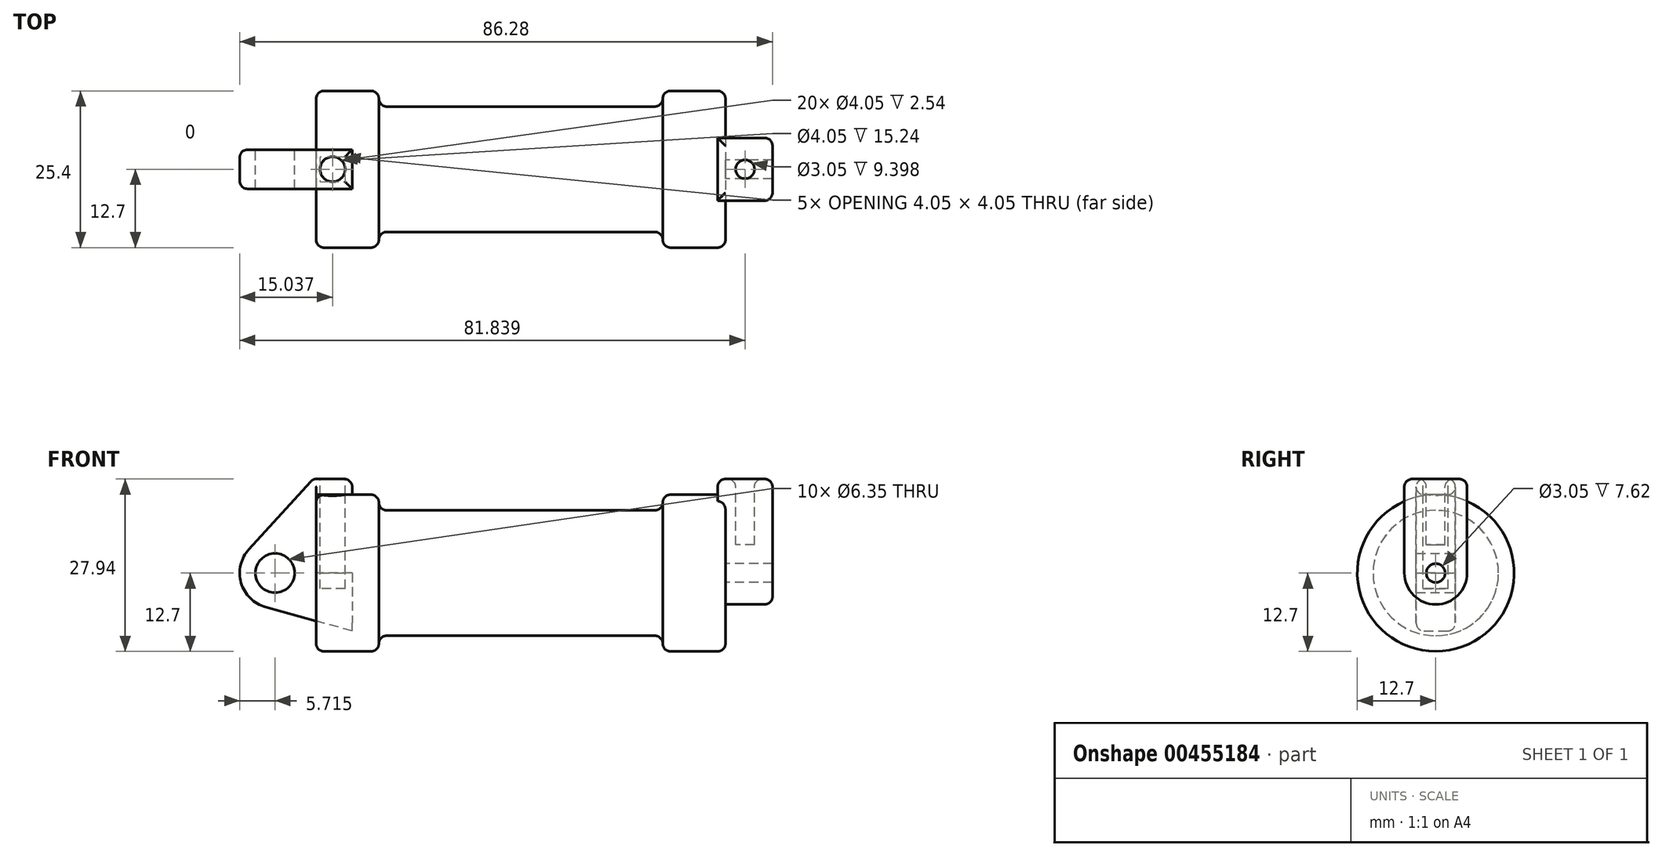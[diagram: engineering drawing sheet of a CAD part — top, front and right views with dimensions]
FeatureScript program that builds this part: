
annotation { "Feature Type Name" : "Feature", "Feature Type Description" : "" }
export const myFeature = defineFeature(function(context is Context, id is Id, definition is map)
    precondition{}
    {
        {
            var Q0;
            Q0=qCreatedBy(makeId("Front.planeOp"),FACE);
            var sketch = newSketch(context, id + "F0", { "sketchPlane" : qUnion([Q0])});
            skLineSegment(sketch, "E0", {"start": v(0, 0) * mm, "end": v(0, 12.7) * mm});
            skLineSegment(sketch, "E1", {"start": v(0, 12.7) * mm, "end": v(10.16, 12.7) * mm});
            skLineSegment(sketch, "E2", {"start": v(10.16, 12.7) * mm, "end": v(10.16, 10.16) * mm});
            skLineSegment(sketch, "E3", {"start": v(10.16, 10.16) * mm, "end": v(56.13, 10.16) * mm});
            skLineSegment(sketch, "E4", {"start": v(56.13, 10.16) * mm, "end": v(56.13, 12.7) * mm});
            skLineSegment(sketch, "E5", {"start": v(56.13, 12.7) * mm, "end": v(66.3, 12.7) * mm});
            skLineSegment(sketch, "E6", {"start": v(66.3, 12.7) * mm, "end": v(66.3, 0) * mm});
            skLineSegment(sketch, "E7", {"start": v(66.3, 0) * mm, "end": v(0, 0) * mm});
            skLineSegment(sketch, "E8", {"start": v(5.84, 15.24) * mm, "end": v(-0.5, 15.24) * mm});
            skLineSegment(sketch, "E9", {"start": v(-0.5, 15.24) * mm, "end": v(-10.88, 3.85) * mm});
            skLineSegment(sketch, "E10", {"start": v(0, 0) * mm, "end": v(-6.65, 0) * mm});
            skCircle(sketch, "E11", {"center": v(-6.65, 0) * mm, "radius": 5.72 * mm});
            skCircle(sketch, "E12", {"center": v(-6.65, 0) * mm, "radius": 3.18 * mm});
            skLineSegment(sketch, "E13", {"start": v(5.84, 15.24) * mm, "end": v(5.84, -9.4) * mm});
            skLineSegment(sketch, "E14", {"start": v(5.84, -9.4) * mm, "end": v(-8.18, -5.5) * mm});
            skSolve(sketch);
        }
        {
            var Q0;
            {var subQ0=sQuery(id+"F0.wireOp",EDGE,"E2");Q0=makeQuery(id+"F0.imprint","IMPRINT",FACE,{"disambiguationData":[TD([[makeQuery(id+"F0.imprint","IMPRINT",EDGE,{"derivedFrom":subQ0}),-1.0]])]});}
            var Q1;
            {var subQ0=sQuery(id+"F0.wireOp",EDGE,"E0");Q1=makeQuery(id+"F0.imprint","IMPRINT",FACE,{"disambiguationData":[TD([[makeQuery(id+"F0.imprint","IMPRINT",EDGE,{"derivedFrom":subQ0}),-1.0]])]});}
            var Q2;
            Q2=sQuery(id+"F0.wireOp",EDGE,"E7");
            revolve(context, id + "F1", {"entities" : qUnion([Q0, Q1]), "axis" : qUnion([Q2]), "revolveType" : RevolveType.FULL});
        }
        {
            var Q0;
            Q0=makeQuery(id+"F1.opRevolve","SWEPT_FACE",FACE,{"disambiguationData":[OSD([sQuery(id+"F0.wireOp",EDGE,"E6")])]});
            var sketch = newSketch(context, id + "F2", { "sketchPlane" : qUnion([Q0])});
            skCircle(sketch, "E15", {"center": v(0, 0) * mm, "radius": 5.08 * mm});
            skCircle(sketch, "E16", {"center": v(0, 0) * mm, "radius": 1.52 * mm});
            skLineSegment(sketch, "E17", {"start": v(0, 0) * mm, "end": v(5.08, 0) * mm});
            skLineSegment(sketch, "E18", {"start": v(5.08, 15.24) * mm, "end": v(5.08, 0) * mm});
            skLineSegment(sketch, "E19", {"start": v(0, 0) * mm, "end": v(-0.8, 0) * mm});
            skLineSegment(sketch, "E20", {"start": v(-5.08, 0) * mm, "end": v(-5.08, 15.24) * mm});
            skLineSegment(sketch, "E21", {"start": v(-5.08, 15.24) * mm, "end": v(5.08, 15.24) * mm});
            skSolve(sketch);
        }
        {
            var Q0;
            Q0=makeQuery(id+"F2.imprint","IMPRINT",FACE,{"disambiguationData":[TD([[makeQuery(id+"F2.imprint","IMPRINT",EDGE,{"derivedFrom":sQuery(id+"F2.wireOp",EDGE,"E16")}),-1.0]])]});
            var Q1;
            {var subQ0=sQuery(id+"F2.wireOp",EDGE,"E18");var subQ1=sQuery(id+"F2.wireOp",EDGE,"E15");var subQ2=makeQuery(id+"F2.imprint","INTERSECT",VERTEX,{"derivedFrom":[subQ1,subQ0]});Q1=makeQuery(id+"F2.imprint","IMPRINT",FACE,{"disambiguationData":[TD([[makeQuery(id+"F2.imprint","IMPRINT",EDGE,{"disambiguationData":[TD([[subQ2,-1.0]])],"derivedFrom":subQ1}),-1.0]])]});}
            var Q2;
            {var subQ0=sQuery(id+"F2.wireOp",EDGE,"E21");Q2=makeQuery(id+"F2.imprint","IMPRINT",FACE,{"disambiguationData":[TD([[makeQuery(id+"F2.imprint","IMPRINT",EDGE,{"derivedFrom":subQ0}),-1.0]])]});}
            extrude(context, id + "F3", {"entities" : qUnion([Q0, Q1, Q2]), "operationType" : NewBodyOperationType.ADD, "oppositeDirection" : true, "depth" : 1.27 * mm});
        }
        {
            var Q0;
            Q0 = qSketchRegion(id + "F2", true);
            extrude(context, id + "F4", {"entities" : qUnion([Q0]), "operationType" : NewBodyOperationType.ADD, "depth" : 7.62 * mm});
        }
        {
            var Q0;
            {var subQ0=sQuery(id+"F2.wireOp",EDGE,"E21");Q0=makeQuery(id+"F4.boolean.opBoolean","MERGE",FACE,{"derivedFrom":[makeQuery(id+"F3.opExtrude","SWEPT_FACE",FACE,{"disambiguationData":[OSD([subQ0])]}),makeQuery(id+"F4.opExtrude","SWEPT_FACE",FACE,{"disambiguationData":[OSD([subQ0])]})]});}
            var sketch = newSketch(context, id + "F5", { "sketchPlane" : qUnion([Q0])});
            skCircle(sketch, "E22", {"center": v(69.47, 0) * mm, "radius": 1.52 * mm});
            skSolve(sketch);
        }
        {
            var Q0;
            {var subQ1=sQuery(id+"F0.wireOp",EDGE,"E0");Q0=makeQuery(id+"F0.imprint","IMPRINT",FACE,{"disambiguationData":[TD([[makeQuery(id+"F0.imprint","IMPRINT",EDGE,{"derivedFrom":subQ1}),1.0]])]});}
            var Q1;
            {var subQ5=sQuery(id+"F0.wireOp",EDGE,"E12");Q1=makeQuery(id+"F0.imprint","IMPRINT",FACE,{"disambiguationData":[TD([[makeQuery(id+"F0.imprint","IMPRINT",EDGE,{"derivedFrom":subQ5}),-1.0]])]});}
            var Q2;
            {var subQ0=sQuery(id+"F0.wireOp",EDGE,"E14");Q2=makeQuery(id+"F0.imprint","IMPRINT",FACE,{"disambiguationData":[TD([[makeQuery(id+"F0.imprint","IMPRINT",EDGE,{"derivedFrom":subQ0}),-1.0]])]});}
            extrude(context, id + "F6", {"entities" : qUnion([Q0, Q1, Q2]), "endBound" : BoundingType.SYMMETRIC, "depth" : 6.35 * mm});
        }
        {
            var Q0;
            Q0=makeQuery(id+"F6.opExtrude","SWEPT_FACE",FACE,{"disambiguationData":[OSD([sQuery(id+"F0.wireOp",EDGE,"E8")])]});
            var sketch = newSketch(context, id + "F7", { "sketchPlane" : qUnion([Q0])});
            skPoint(sketch, "E23.endSnap0", {"position": v(2.67, -3.18) * mm});
            skCircle(sketch, "E24", {"center": v(2.67, 0) * mm, "radius": 2.03 * mm});
            skSolve(sketch);
        }
        {
            var Q0;
            Q0 = qSketchRegion(id + "F7", true);
            extrude(context, id + "F8", {"entities" : qUnion([Q0]), "operationType" : NewBodyOperationType.REMOVE, "oppositeDirection" : true, "depth" : 17.78 * mm});
        }
        {
            var Q0;
            Q0 = qSketchRegion(id + "F5", true);
            extrude(context, id + "F9", {"entities" : qUnion([Q0]), "operationType" : NewBodyOperationType.REMOVE, "oppositeDirection" : true, "depth" : 10.67 * mm});
        }
        {
            var Q0;
            Q0=makeQuery(id+"F6.opExtrude","CAP_EDGE",EDGE,{"disambiguationData":[OSD([sQuery(id+"F0.wireOp",EDGE,"E8")])],"isStart":false});
            var Q1;
            Q1=makeQuery(id+"F6.opExtrude","SWEPT_EDGE",EDGE,{"disambiguationData":[OSD([sQuery(id+"F0.wireOp",EDGE,"E8"),sQuery(id+"F0.wireOp",EDGE,"E13")])]});
            var Q2;
            Q2=makeQuery(id+"F6.opExtrude","CAP_EDGE",EDGE,{"disambiguationData":[OSD([sQuery(id+"F0.wireOp",EDGE,"E8")])],"isStart":true});
            var Q3;
            Q3=makeQuery(id+"F6.opExtrude","SWEPT_EDGE",EDGE,{"disambiguationData":[OSD([sQuery(id+"F0.wireOp",EDGE,"E8"),sQuery(id+"F0.wireOp",EDGE,"E9")])]});
            var Q4;
            Q4=makeQuery(id+"F6.opExtrude","CAP_EDGE",EDGE,{"disambiguationData":[OSD([sQuery(id+"F0.wireOp",EDGE,"E9")])],"isStart":false});
            var Q5;
            Q5=makeQuery(id+"F6.opExtrude","CAP_EDGE",EDGE,{"disambiguationData":[OSD([sQuery(id+"F0.wireOp",EDGE,"E9")])],"isStart":true});
            var Q6;
            Q6=makeQuery(id+"F6.opExtrude","CAP_EDGE",EDGE,{"disambiguationData":[OSD([sQuery(id+"F0.wireOp",EDGE,"E11")])],"isStart":true});
            var Q7;
            Q7=makeQuery(id+"F6.opExtrude","CAP_EDGE",EDGE,{"disambiguationData":[OSD([sQuery(id+"F0.wireOp",EDGE,"E11")])],"isStart":false});
            var Q8;
            Q8=makeQuery(id+"F6.opExtrude","CAP_EDGE",EDGE,{"disambiguationData":[OSD([sQuery(id+"F0.wireOp",EDGE,"E14")])],"isStart":false});
            fillet(context, id + "F10", {"entities" : qUnion([Q0, Q1, Q2, Q3, Q4, Q5, Q6, Q7, Q8]), "radius" : 1.27 * mm, "tangentPropagation" : true, "allowEdgeOverflow" : false});
        }
        {
            var Q0;
            Q0=makeQuery(id+"F6.opExtrude","CAP_EDGE",EDGE,{"disambiguationData":[OSD([sQuery(id+"F0.wireOp",EDGE,"E1")])],"isStart":false});
            fillet(context, id + "F11", {"entities" : qUnion([Q0]), "radius" : 1.27 * mm, "tangentPropagation" : true, "allowEdgeOverflow" : false});
        }
        {
            var Q0;
            Q0=makeQuery(id+"F6.opExtrude","CAP_EDGE",EDGE,{"disambiguationData":[OSD([sQuery(id+"F0.wireOp",EDGE,"E1")])],"isStart":true});
            fillet(context, id + "F12", {"entities" : qUnion([Q0]), "radius" : 1.27 * mm, "tangentPropagation" : true, "allowEdgeOverflow" : false});
        }
        {
            var Q0;
            Q0=makeQuery(id+"F1.opRevolve","SWEPT_FACE",FACE,{"disambiguationData":[OSD([sQuery(id+"F0.wireOp",EDGE,"E2")])]});
            fillet(context, id + "F13", {"entities" : qUnion([Q0]), "radius" : 1.27 * mm, "tangentPropagation" : true, "allowEdgeOverflow" : false});
        }
        {
            var Q0;
            Q0=makeQuery(id+"F1.opRevolve","SWEPT_FACE",FACE,{"disambiguationData":[OSD([sQuery(id+"F0.wireOp",EDGE,"E4")])]});
            fillet(context, id + "F14", {"entities" : qUnion([Q0]), "radius" : 1.27 * mm, "tangentPropagation" : true, "allowEdgeOverflow" : false});
        }
        {
            var Q0;
            {var subQ0=sQuery(id+"F2.wireOp",EDGE,"E21");var subQ1=sQuery(id+"F2.wireOp",EDGE,"E20");Q0=makeQuery(id+"F4.boolean.opBoolean","MERGE",EDGE,{"derivedFrom":[makeQuery(id+"F3.opExtrude","SWEPT_EDGE",EDGE,{"disambiguationData":[OSD([subQ1,subQ0])]}),makeQuery(id+"F4.opExtrude","SWEPT_EDGE",EDGE,{"disambiguationData":[OSD([subQ1,subQ0])]})]});}
            var Q1;
            Q1=makeQuery(id+"F4.opExtrude","CAP_EDGE",EDGE,{"disambiguationData":[OSD([sQuery(id+"F2.wireOp",EDGE,"E20")])],"isStart":false});
            var Q2;
            Q2=makeQuery(id+"F4.opExtrude","CAP_EDGE",EDGE,{"disambiguationData":[OSD([sQuery(id+"F2.wireOp",EDGE,"E21")])],"isStart":false});
            var Q3;
            {var subQ0=sQuery(id+"F2.wireOp",EDGE,"E21");Q3=makeQuery(id+"F4.boolean.opBoolean","MERGE",FACE,{"derivedFrom":[makeQuery(id+"F3.opExtrude","SWEPT_FACE",FACE,{"disambiguationData":[OSD([subQ0])]}),makeQuery(id+"F4.opExtrude","SWEPT_FACE",FACE,{"disambiguationData":[OSD([subQ0])]})]});}
            var Q4;
            {var subQ0=sQuery(id+"F2.wireOp",EDGE,"E21");var subQ1=sQuery(id+"F2.wireOp",EDGE,"E18");Q4=makeQuery(id+"F4.boolean.opBoolean","MERGE",EDGE,{"derivedFrom":[makeQuery(id+"F3.opExtrude","SWEPT_EDGE",EDGE,{"disambiguationData":[OSD([subQ1,subQ0])]}),makeQuery(id+"F4.opExtrude","SWEPT_EDGE",EDGE,{"disambiguationData":[OSD([subQ1,subQ0])]})]});}
            fillet(context, id + "F15", {"entities" : qUnion([Q0, Q1, Q2, Q3, Q4]), "radius" : 1.27 * mm, "tangentPropagation" : true, "allowEdgeOverflow" : false});
        }
        {
            var Q0;
            Q0=makeQuery(id+"F1.opRevolve","SWEPT_EDGE",EDGE,{"disambiguationData":[OSD([sQuery(id+"F0.wireOp",EDGE,"E5"),sQuery(id+"F0.wireOp",EDGE,"E6")])]});
            var Q1;
            Q1=makeQuery(id+"F1.opRevolve","SWEPT_EDGE",EDGE,{"disambiguationData":[OSD([sQuery(id+"F0.wireOp",EDGE,"E0"),sQuery(id+"F0.wireOp",EDGE,"E1")])]});
            fillet(context, id + "F16", {"entities" : qUnion([Q0, Q1]), "radius" : 1.27 * mm, "tangentPropagation" : true, "allowEdgeOverflow" : false});
        }
    });
